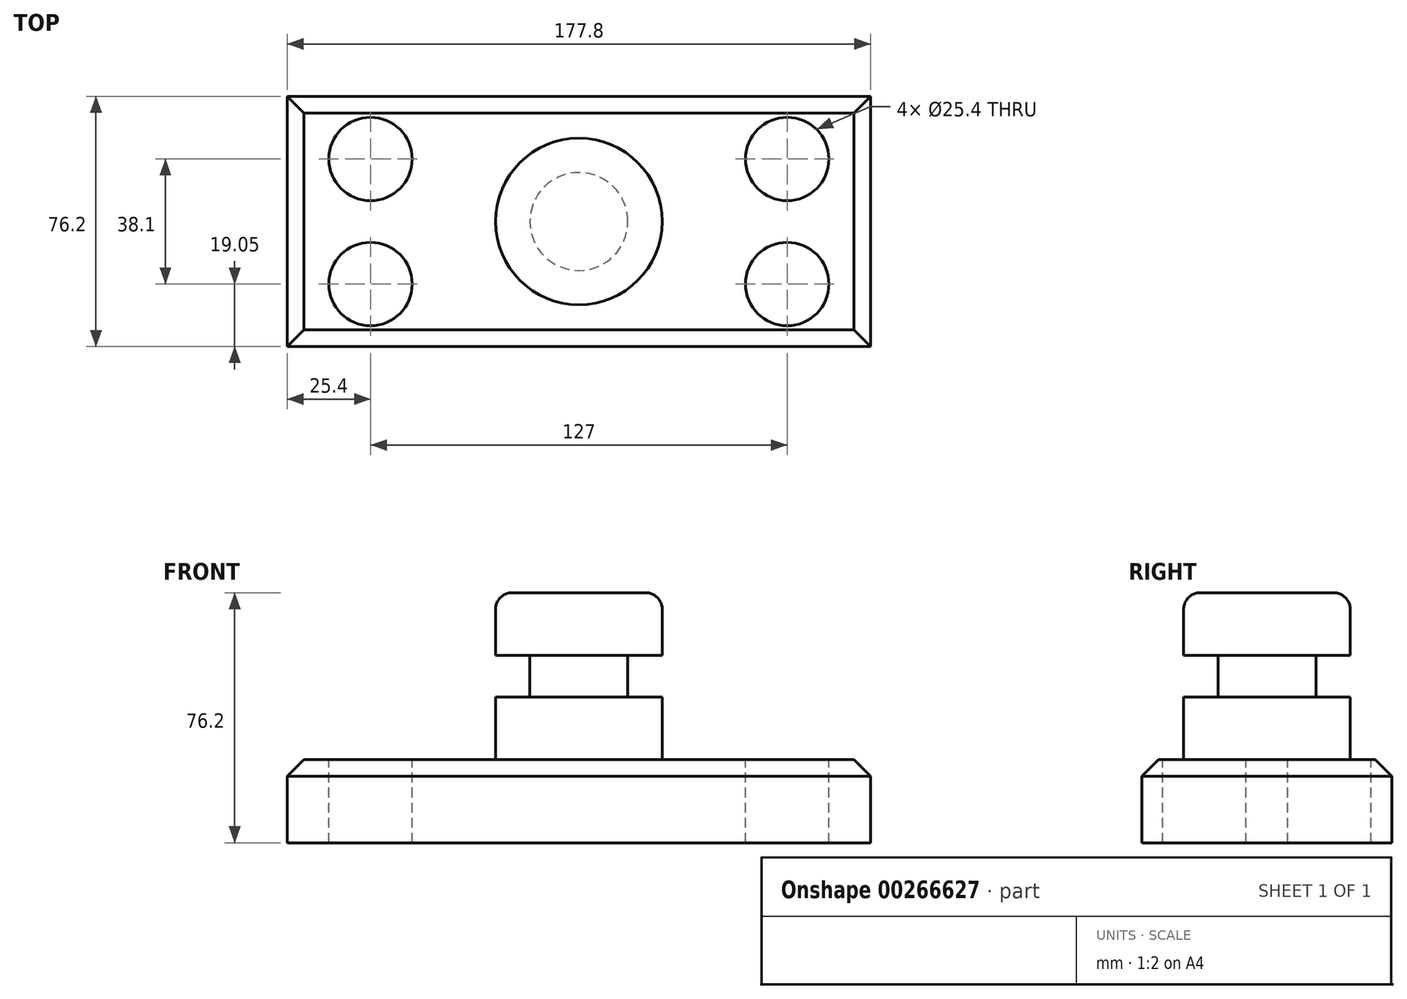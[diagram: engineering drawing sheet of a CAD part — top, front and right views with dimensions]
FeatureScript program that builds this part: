
annotation { "Feature Type Name" : "Feature", "Feature Type Description" : "" }
export const myFeature = defineFeature(function(context is Context, id is Id, definition is map)
    precondition{}
    {
        {
            var Q0;
            Q0=qCreatedBy(makeId("Top.planeOp"),FACE);
            var sketch = newSketch(context, id + "F0", { "sketchPlane" : qUnion([Q0])});
            skLineSegment(sketch, "E0.bottom", {"start": v(-88.9, 38.1) * mm, "end": v(88.9, 38.1) * mm});
            skLineSegment(sketch, "E0.top", {"start": v(-88.9, -38.1) * mm, "end": v(88.9, -38.1) * mm});
            skLineSegment(sketch, "E0.left", {"start": v(-88.9, 38.1) * mm, "end": v(-88.9, -38.1) * mm});
            skLineSegment(sketch, "E0.right", {"start": v(88.9, 38.1) * mm, "end": v(88.9, -38.1) * mm});
            skPoint(sketch, "E0.middle", {"position": v(0, 0) * mm});
            skSolve(sketch);
        }
        {
            var Q0;
            Q0=makeQuery(id+"F0.imprint","IMPRINT",FACE,{"disambiguationData":[TD([[makeQuery(id+"F0.imprint","IMPRINT",EDGE,{"derivedFrom":sQuery(id+"F0.wireOp",EDGE,"E0.bottom")}),-1.0]])]});
            extrude(context, id + "F1", {"entities" : qUnion([Q0]), "depth" : 25.4 * mm});
        }
        {
            var Q0;
            Q0=makeQuery(id+"F1.opExtrude","CAP_FACE",FACE,{"disambiguationData":[OSD([sQuery(id+"F0.wireOp",EDGE,"E0.bottom"),sQuery(id+"F0.wireOp",EDGE,"E0.top"),sQuery(id+"F0.wireOp",EDGE,"E0.left"),sQuery(id+"F0.wireOp",EDGE,"E0.right")])],"isStart":false});
            var sketch = newSketch(context, id + "F2", { "sketchPlane" : qUnion([Q0])});
            skCircle(sketch, "E1", {"center": v(-63.5, 19.05) * mm, "radius": 12.7 * mm});
            skCircle(sketch, "E2", {"center": v(-63.5, -19.05) * mm, "radius": 12.7 * mm});
            skCircle(sketch, "E3", {"center": v(63.5, -19.05) * mm, "radius": 12.7 * mm});
            skCircle(sketch, "E4", {"center": v(63.5, 19.05) * mm, "radius": 12.7 * mm});
            skSolve(sketch);
        }
        {
            var Q0;
            Q0 = qSketchRegion(id + "F2", true);
            extrude(context, id + "F3", {"entities" : qUnion([Q0]), "operationType" : NewBodyOperationType.REMOVE, "endBound" : BoundingType.THROUGH_ALL, "oppositeDirection" : true, "depth" : 25.4 * mm});
        }
        {
            var Q0;
            Q0=qCreatedBy(makeId("Front.planeOp"),FACE);
            var sketch = newSketch(context, id + "F4", { "sketchPlane" : qUnion([Q0])});
            skLineSegment(sketch, "E5.bottom", {"start": v(0, 25.4) * mm, "end": v(-25.4, 25.4) * mm});
            skLineSegment(sketch, "E5.top", {"start": v(0, 76.2) * mm, "end": v(-25.4, 76.2) * mm});
            skLineSegment(sketch, "E5.left", {"start": v(0, 25.4) * mm, "end": v(0, 76.2) * mm});
            skLineSegment(sketch, "E5.right", {"start": v(-25.4, 25.4) * mm, "end": v(-25.4, 76.2) * mm});
            skSolve(sketch);
        }
        {
            var Q0;
            Q0=makeQuery(id+"F4.imprint","IMPRINT",FACE,{"disambiguationData":[TD([[makeQuery(id+"F4.imprint","IMPRINT",EDGE,{"derivedFrom":sQuery(id+"F4.wireOp",EDGE,"E5.bottom")}),-1.0]])]});
            var Q1;
            Q1=sQuery(id+"F4.wireOp",EDGE,"E5.left");
            revolve(context, id + "F5", {"operationType" : NewBodyOperationType.ADD, "entities" : qUnion([Q0]), "axis" : qUnion([Q1]), "revolveType" : RevolveType.FULL});
        }
        {
            var Q0;
            Q0=qCreatedBy(makeId("Front.planeOp"),FACE);
            var sketch = newSketch(context, id + "F6", { "sketchPlane" : qUnion([Q0])});
            skLineSegment(sketch, "E6.bottom", {"start": v(-33.97, 57.15) * mm, "end": v(-14.92, 57.15) * mm});
            skLineSegment(sketch, "E6.top", {"start": v(-33.97, 44.45) * mm, "end": v(-14.92, 44.45) * mm});
            skLineSegment(sketch, "E6.left", {"start": v(-33.97, 57.15) * mm, "end": v(-33.97, 44.45) * mm});
            skLineSegment(sketch, "E6.right", {"start": v(-14.92, 57.15) * mm, "end": v(-14.92, 44.45) * mm});
            skSolve(sketch);
        }
        {
            var Q0;
            Q0=makeQuery(id+"F6.imprint","IMPRINT",FACE,{"disambiguationData":[TD([[makeQuery(id+"F6.imprint","IMPRINT",EDGE,{"derivedFrom":sQuery(id+"F6.wireOp",EDGE,"E6.bottom")}),-1.0]])]});
            var Q1;
            Q1=makeQuery(id+"F5.opRevolve","SWEPT_EDGE",EDGE,{"disambiguationData":[OSD([sQuery(id+"F4.wireOp",EDGE,"E5.top"),sQuery(id+"F4.wireOp",EDGE,"E5.right")])]});
            revolve(context, id + "F7", {"operationType" : NewBodyOperationType.REMOVE, "entities" : qUnion([Q0]), "axis" : qUnion([Q1]), "revolveType" : RevolveType.FULL, "oppositeDirection" : true});
        }
        {
            var Q0;
            Q0=makeQuery(id+"F5.opRevolve","SWEPT_EDGE",EDGE,{"disambiguationData":[OSD([sQuery(id+"F4.wireOp",EDGE,"E5.bottom"),sQuery(id+"F4.wireOp",EDGE,"E5.right")])]});
            var Q1;
            Q1=makeQuery(id+"F5.opRevolve","SWEPT_EDGE",EDGE,{"disambiguationData":[OSD([sQuery(id+"F4.wireOp",EDGE,"E5.top"),sQuery(id+"F4.wireOp",EDGE,"E5.right")])]});
            fillet(context, id + "F8", {"entities" : qUnion([Q0, Q1]), "radius" : 5.08 * mm, "tangentPropagation" : true, "allowEdgeOverflow" : false});
        }
        {
            var Q0;
            Q0=makeQuery(id+"F1.opExtrude","CAP_EDGE",EDGE,{"disambiguationData":[OSD([sQuery(id+"F0.wireOp",EDGE,"E0.left")])],"isStart":false});
            var Q1;
            Q1=makeQuery(id+"F1.opExtrude","CAP_EDGE",EDGE,{"disambiguationData":[OSD([sQuery(id+"F0.wireOp",EDGE,"E0.top")])],"isStart":false});
            var Q2;
            Q2=makeQuery(id+"F1.opExtrude","CAP_EDGE",EDGE,{"disambiguationData":[OSD([sQuery(id+"F0.wireOp",EDGE,"E0.bottom")])],"isStart":false});
            var Q3;
            Q3=makeQuery(id+"F1.opExtrude","CAP_EDGE",EDGE,{"disambiguationData":[OSD([sQuery(id+"F0.wireOp",EDGE,"E0.right")])],"isStart":false});
            chamfer(context, id + "F9", {"entities" : qUnion([Q0, Q1, Q2, Q3]), "width" : 5.08 * mm, "tangentPropagation" : true});
        }
    });
